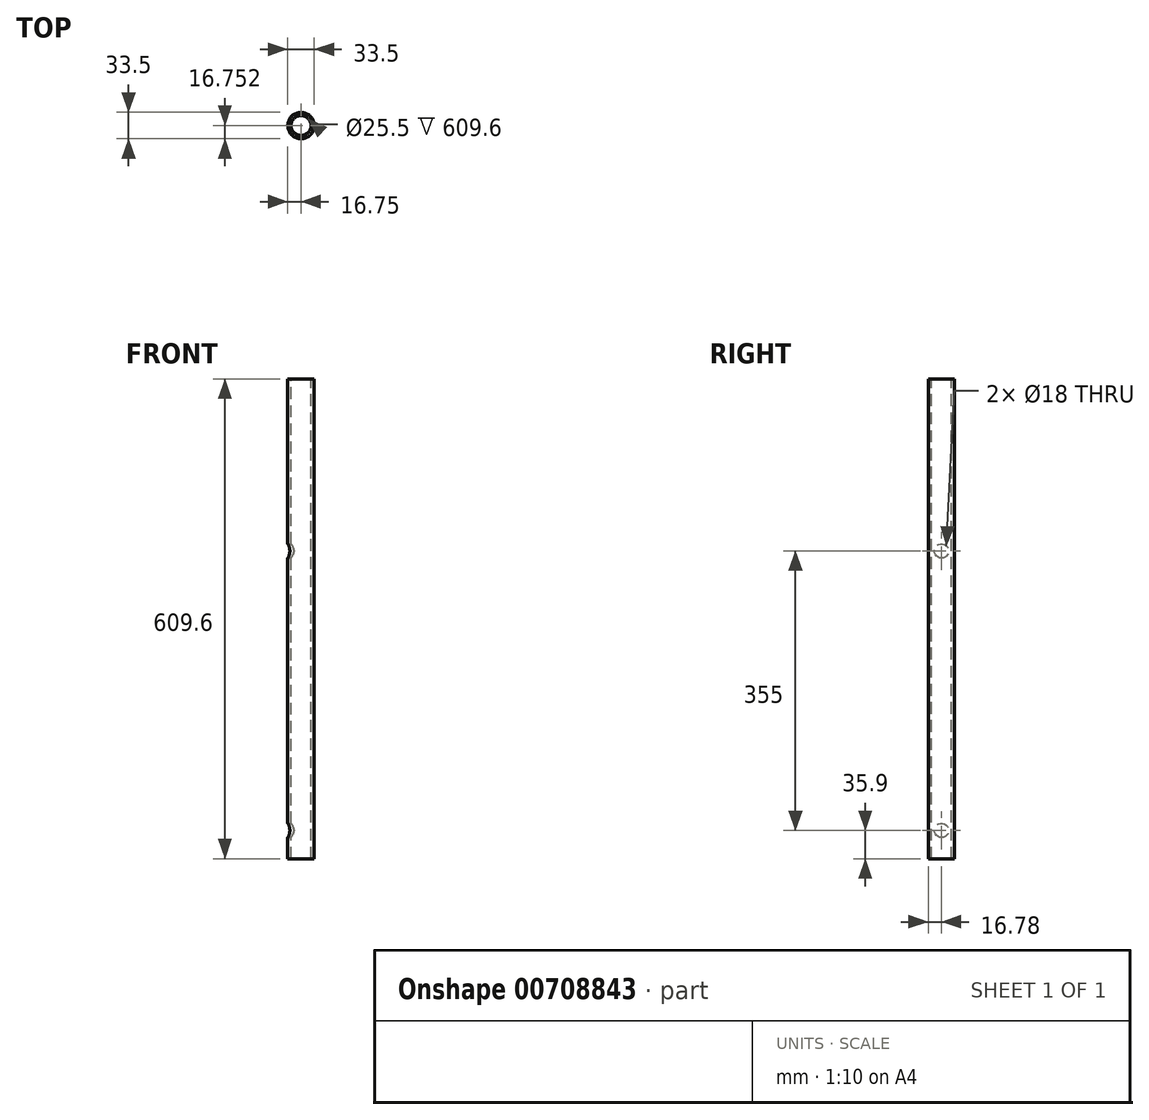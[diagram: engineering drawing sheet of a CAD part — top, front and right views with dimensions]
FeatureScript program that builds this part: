
annotation { "Feature Type Name" : "Feature", "Feature Type Description" : "" }
export const myFeature = defineFeature(function(context is Context, id is Id, definition is map)
    precondition{}
    {
        {
            var Q0;
            Q0=qCreatedBy(makeId("Right.planeOp"),FACE);
            var sketch = newSketch(context, id + "F0", { "sketchPlane" : qUnion([Q0])});
            skLineSegment(sketch, "E0.bottom", {"start": v(12.72, 318.7) * mm, "end": v(16.72, 318.7) * mm});
            skLineSegment(sketch, "E0.top", {"start": v(12.72, -290.9) * mm, "end": v(16.72, -290.9) * mm});
            skLineSegment(sketch, "E0.left", {"start": v(12.72, 318.7) * mm, "end": v(12.72, -290.9) * mm});
            skLineSegment(sketch, "E0.right", {"start": v(16.72, 318.7) * mm, "end": v(16.72, -290.9) * mm});
            skLineSegment(sketch, "E1", {"start": v(-0.03, 318.7) * mm, "end": v(-0.03, -290.9) * mm});
            skSolve(sketch);
        }
        {
            var Q0;
            Q0=makeQuery(id+"F0.imprint","IMPRINT",FACE,{"disambiguationData":[TD([[makeQuery(id+"F0.imprint","IMPRINT",EDGE,{"derivedFrom":sQuery(id+"F0.wireOp",EDGE,"E0.bottom")}),-1.0]])]});
            var Q1;
            Q1=sQuery(id+"F0.wireOp",EDGE,"E1");
            revolve(context, id + "F1", {"surfaceOperationType" : NewSurfaceOperationType.NEW, "entities" : qUnion([Q0]), "axis" : qUnion([Q1]), "revolveType" : RevolveType.FULL});
        }
        {
            var Q0;
            Q0=qCreatedBy(makeId("Right.planeOp"),FACE);
            var sketch = newSketch(context, id + "F2", { "sketchPlane" : qUnion([Q0])});
            skCircle(sketch, "E2", {"center": v(0, 100) * mm, "radius": 9 * mm});
            skCircle(sketch, "E3", {"center": v(0, -255) * mm, "radius": 9 * mm});
            skSolve(sketch);
        }
        {
            var Q0;
            Q0=qSketchRegion(id+"F2",true);
            extrude(context, id + "F3", {"entities" : qUnion([Q0]), "operationType" : NewBodyOperationType.REMOVE, "endBound" : BoundingType.THROUGH_ALL, "oppositeDirection" : true, "depth" : 0 * mm, "offsetDistance" : 25 * mm});
        }
    });
